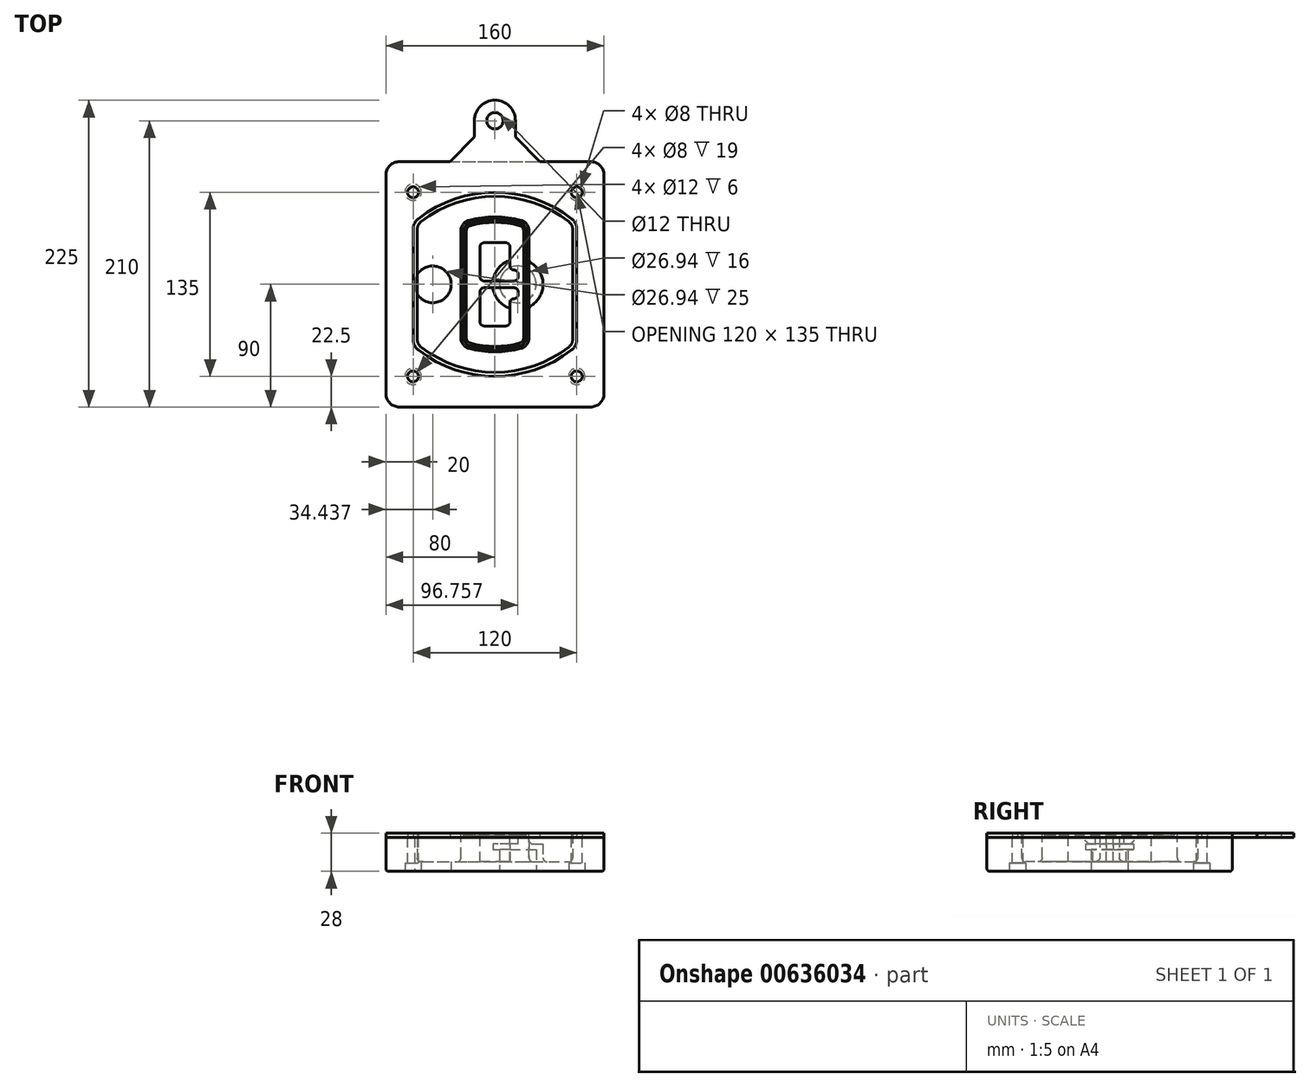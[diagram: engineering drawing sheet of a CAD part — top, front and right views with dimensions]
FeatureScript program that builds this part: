
annotation { "Feature Type Name" : "Feature", "Feature Type Description" : "" }
export const myFeature = defineFeature(function(context is Context, id is Id, definition is map)
    precondition{}
    {
        {
            var Q0;
            Q0=qCreatedBy(makeId("Top.planeOp"),FACE);
            var sketch = newSketch(context, id + "F0", { "sketchPlane" : qUnion([Q0])});
            skPoint(sketch, "E0.rect.middle", {"position": v(0, 0) * mm});
            skLineSegment(sketch, "E1.bottom", {"start": v(-70, -90) * mm, "end": v(70, -90) * mm});
            skLineSegment(sketch, "E1.top", {"start": v(-70, 90) * mm, "end": v(70, 90) * mm});
            skLineSegment(sketch, "E1.left", {"start": v(-80, -80) * mm, "end": v(-80, 80) * mm});
            skLineSegment(sketch, "E1.right", {"start": v(80, -80) * mm, "end": v(80, 80) * mm});
            skLineSegment(sketch, "E2", {"start": v(-80, 90) * mm, "end": v(80, -90) * mm, "construction": true});
            skLineSegment(sketch, "E3", {"start": v(80, 90) * mm, "end": v(-80, -90) * mm, "construction": true});
            skCircle(sketch, "E4", {"center": v(-60, 67.5) * mm, "radius": 4 * mm});
            skCircle(sketch, "E5", {"center": v(60, 67.5) * mm, "radius": 4 * mm});
            skCircle(sketch, "E6", {"center": v(60, -67.5) * mm, "radius": 4 * mm});
            skCircle(sketch, "E7", {"center": v(-60, -67.5) * mm, "radius": 4 * mm});
            skLineSegment(sketch, "E8", {"start": v(-60, 67.5) * mm, "end": v(60, 67.5) * mm, "construction": true});
            skLineSegment(sketch, "E9", {"start": v(60, 67.5) * mm, "end": v(60, -67.5) * mm, "construction": true});
            skLineSegment(sketch, "E10", {"start": v(60, -67.5) * mm, "end": v(-60, -67.5) * mm, "construction": true});
            skLineSegment(sketch, "E11", {"start": v(-60, -67.5) * mm, "end": v(-60, 67.5) * mm, "construction": true});
            skLineSegment(sketch, "E12", {"start": v(-60, 40.3) * mm, "end": v(-60, -40.3) * mm});
            skLineSegment(sketch, "E13", {"start": v(60, 40.3) * mm, "end": v(60, -40.3) * mm});
            skArc(sketch, "E14", {"start": v(56.15, 48.18) * mm, "mid": v(0, 67.5) * mm, "end": v(-56.15, 48.18) * mm});
            skArc(sketch, "E15", {"start": v(-56.15, -48.18) * mm, "mid": v(0, -67.5) * mm, "end": v(56.15, -48.18) * mm});
            skLineSegment(sketch, "E16", {"start": v(-60, 0) * mm, "end": v(60, 0) * mm, "construction": true});
            skPoint(sketch, "E17.visualSharp", {"position": v(-60, -45) * mm});
            skArc(sketch, "E17.filletArc", {"start": v(-60, -40.3) * mm, "mid": v(-58.99, -44.68) * mm, "end": v(-56.15, -48.18) * mm});
            skPoint(sketch, "E18.visualSharp", {"position": v(-60, 45) * mm});
            skArc(sketch, "E18.filletArc", {"start": v(-56.15, 48.18) * mm, "mid": v(-58.99, 44.68) * mm, "end": v(-60, 40.3) * mm});
            skPoint(sketch, "E19.visualSharp", {"position": v(60, 45) * mm});
            skArc(sketch, "E19.filletArc", {"start": v(60, 40.3) * mm, "mid": v(58.99, 44.68) * mm, "end": v(56.15, 48.18) * mm});
            skPoint(sketch, "E20.visualSharp", {"position": v(60, -45) * mm});
            skArc(sketch, "E20.filletArc", {"start": v(56.15, -48.18) * mm, "mid": v(58.99, -44.68) * mm, "end": v(60, -40.3) * mm});
            skPoint(sketch, "E21.visualSharp", {"position": v(-80, 90) * mm});
            skArc(sketch, "E21.filletArc", {"start": v(-70, 90) * mm, "mid": v(-77.07, 87.07) * mm, "end": v(-80, 80) * mm});
            skPoint(sketch, "E22.visualSharp", {"position": v(80, 90) * mm});
            skArc(sketch, "E22.filletArc", {"start": v(80, 80) * mm, "mid": v(77.07, 87.07) * mm, "end": v(70, 90) * mm});
            skPoint(sketch, "E23.visualSharp", {"position": v(80, -90) * mm});
            skArc(sketch, "E23.filletArc", {"start": v(70, -90) * mm, "mid": v(77.07, -87.07) * mm, "end": v(80, -80) * mm});
            skPoint(sketch, "E24.visualSharp", {"position": v(-80, -90) * mm});
            skArc(sketch, "E24.filletArc", {"start": v(-80, -80) * mm, "mid": v(-77.07, -87.07) * mm, "end": v(-70, -90) * mm});
            skArc(sketch, "E25.0", {"start": v(57, 40.3) * mm, "mid": v(56.3, 43.36) * mm, "end": v(54.3, 45.81) * mm});
            skLineSegment(sketch, "E25.1", {"start": v(57, 40.3) * mm, "end": v(57, -40.3) * mm});
            skArc(sketch, "E25.2", {"start": v(54.3, -45.81) * mm, "mid": v(56.3, -43.36) * mm, "end": v(57, -40.3) * mm});
            skArc(sketch, "E25.3", {"start": v(-54.3, -45.81) * mm, "mid": v(0, -64.5) * mm, "end": v(54.3, -45.81) * mm});
            skArc(sketch, "E25.4", {"start": v(-57, -40.3) * mm, "mid": v(-56.3, -43.36) * mm, "end": v(-54.3, -45.81) * mm});
            skArc(sketch, "E25.5", {"start": v(54.3, 45.81) * mm, "mid": v(0, 64.5) * mm, "end": v(-54.3, 45.81) * mm});
            skLineSegment(sketch, "E25.6", {"start": v(-57, 40.3) * mm, "end": v(-57, -40.3) * mm});
            skArc(sketch, "E25.7", {"start": v(-54.3, 45.81) * mm, "mid": v(-56.3, 43.36) * mm, "end": v(-57, 40.3) * mm});
            skArc(sketch, "E26.0", {"start": v(-58.62, 51.33) * mm, "mid": v(-62.58, 46.43) * mm, "end": v(-64, 40.3) * mm});
            skArc(sketch, "E26.1", {"start": v(58.62, 51.33) * mm, "mid": v(0, 71.5) * mm, "end": v(-58.62, 51.33) * mm});
            skArc(sketch, "E26.2", {"start": v(64, 40.3) * mm, "mid": v(62.58, 46.43) * mm, "end": v(58.62, 51.33) * mm});
            skLineSegment(sketch, "E26.3", {"start": v(64, 40.3) * mm, "end": v(64, -40.3) * mm});
            skArc(sketch, "E26.4", {"start": v(58.62, -51.33) * mm, "mid": v(62.58, -46.43) * mm, "end": v(64, -40.3) * mm});
            skLineSegment(sketch, "E26.5", {"start": v(-64, 40.3) * mm, "end": v(-64, -40.3) * mm});
            skArc(sketch, "E26.6", {"start": v(-58.62, -51.33) * mm, "mid": v(0, -71.5) * mm, "end": v(58.62, -51.33) * mm});
            skArc(sketch, "E26.7", {"start": v(-64, -40.3) * mm, "mid": v(-62.58, -46.43) * mm, "end": v(-58.62, -51.33) * mm});
            skSolve(sketch);
        }
        {
            var Q0;
            Q0=makeQuery(id+"F0.imprint","IMPRINT",FACE,{"disambiguationData":[TD([[makeQuery(id+"F0.imprint","IMPRINT",EDGE,{"derivedFrom":sQuery(id+"F0.wireOp",EDGE,"E1.bottom")}),1.0]])]});
            var Q1;
            Q1=makeQuery(id+"F0.imprint","IMPRINT",FACE,{"disambiguationData":[TD([[makeQuery(id+"F0.imprint","IMPRINT",EDGE,{"derivedFrom":sQuery(id+"F0.wireOp",EDGE,"E12")}),1.0]])]});
            var Q2;
            Q2=makeQuery(id+"F0.imprint","IMPRINT",FACE,{"disambiguationData":[TD([[makeQuery(id+"F0.imprint","IMPRINT",EDGE,{"derivedFrom":sQuery(id+"F0.wireOp",EDGE,"E25.0")}),1.0]])]});
            var Q3;
            Q3=makeQuery(id+"F0.imprint","IMPRINT",FACE,{"disambiguationData":[TD([[makeQuery(id+"F0.imprint","IMPRINT",EDGE,{"derivedFrom":sQuery(id+"F0.wireOp",EDGE,"E12")}),-1.0]])]});
            extrude(context, id + "F1", {"entities" : qUnion([Q0, Q1, Q2, Q3]), "oppositeDirection" : true, "depth" : 25 * mm});
        }
        {
            var Q0;
            Q0=makeQuery(id+"F0.imprint","IMPRINT",FACE,{"disambiguationData":[TD([[makeQuery(id+"F0.imprint","IMPRINT",EDGE,{"derivedFrom":sQuery(id+"F0.wireOp",EDGE,"E12")}),1.0]])]});
            extrude(context, id + "F2", {"entities" : qUnion([Q0]), "operationType" : NewBodyOperationType.ADD, "depth" : 3 * mm});
        }
        {
            var Q0;
            Q0=makeQuery(id+"F0.imprint","IMPRINT",FACE,{"disambiguationData":[TD([[makeQuery(id+"F0.imprint","IMPRINT",EDGE,{"derivedFrom":sQuery(id+"F0.wireOp",EDGE,"E25.0")}),1.0]])]});
            extrude(context, id + "F3", {"entities" : qUnion([Q0]), "operationType" : NewBodyOperationType.REMOVE, "oppositeDirection" : true, "depth" : 18 * mm});
        }
        {
            var Q0;
            Q0=makeQuery(id+"F2.opExtrude","CAP_FACE",FACE,{"disambiguationData":[OSD([sQuery(id+"F0.wireOp",EDGE,"E12"),sQuery(id+"F0.wireOp",EDGE,"E13"),sQuery(id+"F0.wireOp",EDGE,"E14"),sQuery(id+"F0.wireOp",EDGE,"E15"),sQuery(id+"F0.wireOp",EDGE,"E17.filletArc"),sQuery(id+"F0.wireOp",EDGE,"E18.filletArc"),sQuery(id+"F0.wireOp",EDGE,"E19.filletArc"),sQuery(id+"F0.wireOp",EDGE,"E20.filletArc"),sQuery(id+"F0.wireOp",EDGE,"E25.0"),sQuery(id+"F0.wireOp",EDGE,"E25.1"),sQuery(id+"F0.wireOp",EDGE,"E25.2"),sQuery(id+"F0.wireOp",EDGE,"E25.3"),sQuery(id+"F0.wireOp",EDGE,"E25.4"),sQuery(id+"F0.wireOp",EDGE,"E25.5"),sQuery(id+"F0.wireOp",EDGE,"E25.6"),sQuery(id+"F0.wireOp",EDGE,"E25.7")])],"isStart":false});
            var sketch = newSketch(context, id + "F4", { "sketchPlane" : qUnion([Q0])});
            skArc(sketch, "E27.0", {"start": v(-19.08, -46.97) * mm, "mid": v(0, -49.5) * mm, "end": v(19.08, -46.97) * mm});
            skArc(sketch, "E28.0", {"start": v(19.08, 46.97) * mm, "mid": v(0, 49.5) * mm, "end": v(-19.08, 46.97) * mm});
            skLineSegment(sketch, "E29", {"start": v(-25, 39.25) * mm, "end": v(-25, -39.25) * mm});
            skLineSegment(sketch, "E30", {"start": v(25, 39.25) * mm, "end": v(25, -39.25) * mm});
            skLineSegment(sketch, "E31", {"start": v(-25, 45.1) * mm, "end": v(25, 45.1) * mm, "construction": true});
            skLineSegment(sketch, "E32", {"start": v(-25, -45.1) * mm, "end": v(25, -45.1) * mm, "construction": true});
            skPoint(sketch, "E33.visualSharp", {"position": v(-25, 45.1) * mm});
            skArc(sketch, "E33.filletArc", {"start": v(-19.08, 46.97) * mm, "mid": v(-23.35, 44.11) * mm, "end": v(-25, 39.25) * mm});
            skPoint(sketch, "E34.visualSharp", {"position": v(25, 45.1) * mm});
            skArc(sketch, "E34.filletArc", {"start": v(25, 39.25) * mm, "mid": v(23.35, 44.11) * mm, "end": v(19.08, 46.97) * mm});
            skPoint(sketch, "E35.visualSharp", {"position": v(25, -45.1) * mm});
            skArc(sketch, "E35.filletArc", {"start": v(19.08, -46.97) * mm, "mid": v(23.35, -44.11) * mm, "end": v(25, -39.25) * mm});
            skPoint(sketch, "E36.visualSharp", {"position": v(-25, -45.1) * mm});
            skArc(sketch, "E36.filletArc", {"start": v(-25, -39.25) * mm, "mid": v(-23.35, -44.11) * mm, "end": v(-19.08, -46.97) * mm});
            skArc(sketch, "E37.0", {"start": v(54.3, 45.81) * mm, "mid": v(0, 64.5) * mm, "end": v(-54.3, 45.81) * mm});
            skArc(sketch, "E37.1", {"start": v(-54.3, 45.81) * mm, "mid": v(-56.3, 43.36) * mm, "end": v(-57, 40.3) * mm});
            skLineSegment(sketch, "E37.2", {"start": v(-57, 40.3) * mm, "end": v(-57, -40.3) * mm});
            skArc(sketch, "E37.3", {"start": v(-57, -40.3) * mm, "mid": v(-56.3, -43.36) * mm, "end": v(-54.3, -45.81) * mm});
            skArc(sketch, "E37.4", {"start": v(-54.3, -45.81) * mm, "mid": v(0, -64.5) * mm, "end": v(54.3, -45.81) * mm});
            skArc(sketch, "E37.5", {"start": v(54.3, -45.81) * mm, "mid": v(56.3, -43.36) * mm, "end": v(57, -40.3) * mm});
            skLineSegment(sketch, "E37.6", {"start": v(57, 40.3) * mm, "end": v(57, -40.3) * mm});
            skArc(sketch, "E37.7", {"start": v(57, 40.3) * mm, "mid": v(56.3, 43.36) * mm, "end": v(54.3, 45.81) * mm});
            skLineSegment(sketch, "E38.0", {"start": v(23, 39.25) * mm, "end": v(23, -39.25) * mm});
            skArc(sketch, "E38.1", {"start": v(18.56, -45.04) * mm, "mid": v(21.76, -42.9) * mm, "end": v(23, -39.25) * mm});
            skArc(sketch, "E38.2", {"start": v(-18.56, -45.04) * mm, "mid": v(0, -47.5) * mm, "end": v(18.56, -45.04) * mm});
            skArc(sketch, "E38.3", {"start": v(-23, -39.25) * mm, "mid": v(-21.76, -42.9) * mm, "end": v(-18.56, -45.04) * mm});
            skLineSegment(sketch, "E38.4", {"start": v(-23, 39.25) * mm, "end": v(-23, -39.25) * mm});
            skArc(sketch, "E38.5", {"start": v(23, 39.25) * mm, "mid": v(21.76, 42.9) * mm, "end": v(18.56, 45.04) * mm});
            skArc(sketch, "E38.6", {"start": v(-18.56, 45.04) * mm, "mid": v(-21.76, 42.9) * mm, "end": v(-23, 39.25) * mm});
            skArc(sketch, "E38.7", {"start": v(18.56, 45.04) * mm, "mid": v(0, 47.5) * mm, "end": v(-18.56, 45.04) * mm});
            skArc(sketch, "E39.0", {"start": v(21, 39.25) * mm, "mid": v(20.18, 41.68) * mm, "end": v(18.04, 43.1) * mm});
            skLineSegment(sketch, "E39.1", {"start": v(21, 39.25) * mm, "end": v(21, -39.25) * mm});
            skArc(sketch, "E39.2", {"start": v(18.04, -43.1) * mm, "mid": v(20.18, -41.68) * mm, "end": v(21, -39.25) * mm});
            skArc(sketch, "E39.3", {"start": v(-18.04, -43.1) * mm, "mid": v(0, -45.5) * mm, "end": v(18.04, -43.1) * mm});
            skArc(sketch, "E39.4", {"start": v(-21, -39.25) * mm, "mid": v(-20.18, -41.68) * mm, "end": v(-18.04, -43.1) * mm});
            skArc(sketch, "E39.5", {"start": v(18.04, 43.1) * mm, "mid": v(0, 45.5) * mm, "end": v(-18.04, 43.1) * mm});
            skLineSegment(sketch, "E39.6", {"start": v(-21, 39.25) * mm, "end": v(-21, -39.25) * mm});
            skArc(sketch, "E39.7", {"start": v(-18.04, 43.1) * mm, "mid": v(-20.18, 41.68) * mm, "end": v(-21, 39.25) * mm});
            skLineSegment(sketch, "E40", {"start": v(-25, 0) * mm, "end": v(25, 0) * mm, "construction": true});
            skLineSegment(sketch, "E41", {"start": v(-11, 5.5) * mm, "end": v(-11, 27.5) * mm});
            skLineSegment(sketch, "E42", {"start": v(-8, 30.5) * mm, "end": v(8, 30.5) * mm});
            skLineSegment(sketch, "E43", {"start": v(11, 27.5) * mm, "end": v(11, 13.5) * mm});
            skLineSegment(sketch, "E44", {"start": v(14, 10.5) * mm, "end": v(14, 10.5) * mm});
            skLineSegment(sketch, "E45", {"start": v(17, 7.5) * mm, "end": v(17, 5.5) * mm});
            skLineSegment(sketch, "E46", {"start": v(14, 2.5) * mm, "end": v(-8, 2.5) * mm});
            skPoint(sketch, "E47.visualSharp", {"position": v(-11, 30.5) * mm});
            skArc(sketch, "E47.filletArc", {"start": v(-8, 30.5) * mm, "mid": v(-10.12, 29.62) * mm, "end": v(-11, 27.5) * mm});
            skPoint(sketch, "E48.visualSharp", {"position": v(11, 30.5) * mm});
            skArc(sketch, "E48.filletArc", {"start": v(11, 27.5) * mm, "mid": v(10.12, 29.62) * mm, "end": v(8, 30.5) * mm});
            skPoint(sketch, "E49.visualSharp", {"position": v(11, 10.5) * mm});
            skArc(sketch, "E49.filletArc", {"start": v(11, 13.5) * mm, "mid": v(11.88, 11.38) * mm, "end": v(14, 10.5) * mm});
            skPoint(sketch, "E50.visualSharp", {"position": v(17, 10.5) * mm});
            skArc(sketch, "E50.filletArc", {"start": v(17, 7.5) * mm, "mid": v(16.12, 9.62) * mm, "end": v(14, 10.5) * mm});
            skPoint(sketch, "E51.visualSharp", {"position": v(17, 2.5) * mm});
            skArc(sketch, "E51.filletArc", {"start": v(14, 2.5) * mm, "mid": v(16.12, 3.38) * mm, "end": v(17, 5.5) * mm});
            skPoint(sketch, "E52.visualSharp", {"position": v(-11, 2.5) * mm});
            skArc(sketch, "E52.filletArc", {"start": v(-11, 5.5) * mm, "mid": v(-10.12, 3.38) * mm, "end": v(-8, 2.5) * mm});
            skLineSegment(sketch, "E53.0.MirrorCS", {"start": v(14, -2.5) * mm, "end": v(-8, -2.5) * mm});
            skArc(sketch, "E54.0.MirrorCS", {"start": v(-11, -5.5) * mm, "mid": v(-10.12, -3.38) * mm, "end": v(-8, -2.5) * mm});
            skLineSegment(sketch, "E55.0.MirrorCS", {"start": v(-11, -5.5) * mm, "end": v(-11, -27.5) * mm});
            skArc(sketch, "E56.0.MirrorCS", {"start": v(-8, -30.5) * mm, "mid": v(-10.12, -29.62) * mm, "end": v(-11, -27.5) * mm});
            skLineSegment(sketch, "E57.0.MirrorCS", {"start": v(-8, -30.5) * mm, "end": v(8, -30.5) * mm});
            skArc(sketch, "E58.0.MirrorCS", {"start": v(11, -27.5) * mm, "mid": v(10.12, -29.62) * mm, "end": v(8, -30.5) * mm});
            skLineSegment(sketch, "E59.0.MirrorCS", {"start": v(11, -27.5) * mm, "end": v(11, -13.5) * mm});
            skArc(sketch, "E60.0.MirrorCS", {"start": v(11, -13.5) * mm, "mid": v(11.88, -11.38) * mm, "end": v(14, -10.5) * mm});
            skArc(sketch, "E61.0.MirrorCS", {"start": v(17, -7.5) * mm, "mid": v(16.12, -9.62) * mm, "end": v(14, -10.5) * mm});
            skLineSegment(sketch, "E62.0.MirrorCS", {"start": v(17, -7.5) * mm, "end": v(17, -5.5) * mm});
            skArc(sketch, "E63.0.MirrorCS", {"start": v(14, -2.5) * mm, "mid": v(16.12, -3.38) * mm, "end": v(17, -5.5) * mm});
            skSolve(sketch);
        }
        {
            var Q0;
            Q0=makeQuery(id+"F4.imprint","IMPRINT",FACE,{"disambiguationData":[TD([[makeQuery(id+"F4.imprint","IMPRINT",EDGE,{"derivedFrom":sQuery(id+"F4.wireOp",EDGE,"E27.0")}),1.0]])]});
            var Q1;
            Q1=makeQuery(id+"F4.imprint","IMPRINT",FACE,{"disambiguationData":[TD([[makeQuery(id+"F4.imprint","IMPRINT",EDGE,{"derivedFrom":sQuery(id+"F4.wireOp",EDGE,"E38.0")}),-1.0]])]});
            var Q2;
            Q2=makeQuery(id+"F4.imprint","IMPRINT",FACE,{"disambiguationData":[TD([[makeQuery(id+"F4.imprint","IMPRINT",EDGE,{"derivedFrom":sQuery(id+"F4.wireOp",EDGE,"E39.0")}),1.0]])]});
            extrude(context, id + "F5", {"entities" : qUnion([Q0, Q1, Q2]), "operationType" : NewBodyOperationType.ADD, "endBound" : BoundingType.UP_TO_NEXT, "oppositeDirection" : true, "depth" : 25 * mm});
        }
        {
            var Q0;
            Q0=makeQuery(id+"F4.imprint","IMPRINT",FACE,{"disambiguationData":[TD([[makeQuery(id+"F4.imprint","IMPRINT",EDGE,{"derivedFrom":sQuery(id+"F4.wireOp",EDGE,"E38.0")}),-1.0]])]});
            extrude(context, id + "F6", {"entities" : qUnion([Q0]), "operationType" : NewBodyOperationType.REMOVE, "oppositeDirection" : true, "depth" : 2 * mm});
        }
        {
            var Q0;
            Q0=makeQuery(id+"F1.opExtrude","CAP_FACE",FACE,{"disambiguationData":[OSD([sQuery(id+"F0.wireOp",EDGE,"E1.bottom"),sQuery(id+"F0.wireOp",EDGE,"E1.top"),sQuery(id+"F0.wireOp",EDGE,"E1.left"),sQuery(id+"F0.wireOp",EDGE,"E1.right"),sQuery(id+"F0.wireOp",EDGE,"E4"),sQuery(id+"F0.wireOp",EDGE,"E5"),sQuery(id+"F0.wireOp",EDGE,"E6"),sQuery(id+"F0.wireOp",EDGE,"E7"),sQuery(id+"F0.wireOp",EDGE,"E21.filletArc"),sQuery(id+"F0.wireOp",EDGE,"E22.filletArc"),sQuery(id+"F0.wireOp",EDGE,"E23.filletArc"),sQuery(id+"F0.wireOp",EDGE,"E24.filletArc")])],"isStart":false});
            var sketch = newSketch(context, id + "F7", { "sketchPlane" : qUnion([Q0])});
            skCircle(sketch, "E64", {"center": v(16.76, 0) * mm, "radius": 13.47 * mm});
            skCircle(sketch, "E65", {"center": v(-45.56, 0) * mm, "radius": 13.47 * mm});
            skLineSegment(sketch, "E66", {"start": v(80, 0) * mm, "end": v(-80, 0) * mm});
            skCircle(sketch, "E67", {"center": v(16.76, 0) * mm, "radius": 18.47 * mm});
            skCircle(sketch, "E68", {"center": v(60, -67.5) * mm, "radius": 6 * mm});
            skCircle(sketch, "E69", {"center": v(-60, -67.5) * mm, "radius": 6 * mm});
            skCircle(sketch, "E70", {"center": v(-60, 67.5) * mm, "radius": 6 * mm});
            skCircle(sketch, "E71", {"center": v(60, 67.5) * mm, "radius": 6 * mm});
            skSolve(sketch);
        }
        {
            var Q0;
            {var subQ1=sQuery(id+"F7.wireOp",EDGE,"E66");var subQ4=sQuery(id+"F7.wireOp",EDGE,"E64");var subQ6=makeQuery(id+"F7.imprint","INTERSECT",VERTEX,{"disambiguationData":[OD(0.0)],"derivedFrom":[subQ4,subQ1]});Q0=makeQuery(id+"F7.imprint","IMPRINT",FACE,{"disambiguationData":[TD([[makeQuery(id+"F7.imprint","IMPRINT",EDGE,{"disambiguationData":[TD([[subQ6,-1.0]])],"derivedFrom":subQ4}),-1.0]])]});}
            var Q1;
            {var subQ0=sQuery(id+"F7.wireOp",EDGE,"E66");var subQ1=sQuery(id+"F7.wireOp",EDGE,"E64");var subQ3=makeQuery(id+"F7.imprint","INTERSECT",VERTEX,{"disambiguationData":[OD(0.0)],"derivedFrom":[subQ1,subQ0]});Q1=makeQuery(id+"F7.imprint","IMPRINT",FACE,{"disambiguationData":[TD([[makeQuery(id+"F7.imprint","IMPRINT",EDGE,{"disambiguationData":[TD([[subQ3,-1.0]])],"derivedFrom":subQ1}),1.0]])]});}
            var Q2;
            {var subQ0=sQuery(id+"F7.wireOp",EDGE,"E66");var subQ1=sQuery(id+"F7.wireOp",EDGE,"E64");var subQ3=makeQuery(id+"F7.imprint","INTERSECT",VERTEX,{"disambiguationData":[OD(0.0)],"derivedFrom":[subQ1,subQ0]});Q2=makeQuery(id+"F7.imprint","IMPRINT",FACE,{"disambiguationData":[TD([[makeQuery(id+"F7.imprint","IMPRINT",EDGE,{"disambiguationData":[TD([[subQ3,1.0]])],"derivedFrom":subQ1}),1.0]])]});}
            var Q3;
            {var subQ1=sQuery(id+"F7.wireOp",EDGE,"E66");var subQ4=sQuery(id+"F7.wireOp",EDGE,"E64");var subQ6=makeQuery(id+"F7.imprint","INTERSECT",VERTEX,{"disambiguationData":[OD(0.0)],"derivedFrom":[subQ4,subQ1]});Q3=makeQuery(id+"F7.imprint","IMPRINT",FACE,{"disambiguationData":[TD([[makeQuery(id+"F7.imprint","IMPRINT",EDGE,{"disambiguationData":[TD([[subQ6,1.0]])],"derivedFrom":subQ4}),-1.0]])]});}
            extrude(context, id + "F8", {"entities" : qUnion([Q0, Q1, Q2, Q3]), "operationType" : NewBodyOperationType.ADD, "oppositeDirection" : true, "depth" : 20 * mm});
        }
        {
            var Q0;
            {var subQ0=sQuery(id+"F7.wireOp",EDGE,"E66");var subQ1=sQuery(id+"F7.wireOp",EDGE,"E64");var subQ3=makeQuery(id+"F7.imprint","INTERSECT",VERTEX,{"disambiguationData":[OD(0.0)],"derivedFrom":[subQ1,subQ0]});Q0=makeQuery(id+"F7.imprint","IMPRINT",FACE,{"disambiguationData":[TD([[makeQuery(id+"F7.imprint","IMPRINT",EDGE,{"disambiguationData":[TD([[subQ3,-1.0]])],"derivedFrom":subQ1}),1.0]])]});}
            var Q1;
            {var subQ0=sQuery(id+"F7.wireOp",EDGE,"E66");var subQ1=sQuery(id+"F7.wireOp",EDGE,"E64");var subQ3=makeQuery(id+"F7.imprint","INTERSECT",VERTEX,{"disambiguationData":[OD(0.0)],"derivedFrom":[subQ1,subQ0]});Q1=makeQuery(id+"F7.imprint","IMPRINT",FACE,{"disambiguationData":[TD([[makeQuery(id+"F7.imprint","IMPRINT",EDGE,{"disambiguationData":[TD([[subQ3,1.0]])],"derivedFrom":subQ1}),1.0]])]});}
            extrude(context, id + "F9", {"entities" : qUnion([Q0, Q1]), "operationType" : NewBodyOperationType.REMOVE, "oppositeDirection" : true, "depth" : 16 * mm});
        }
        {
            var Q0;
            {var subQ0=sQuery(id+"F7.wireOp",EDGE,"E66");var subQ1=sQuery(id+"F7.wireOp",EDGE,"E65");var subQ3=makeQuery(id+"F7.imprint","INTERSECT",VERTEX,{"disambiguationData":[OD(0.0)],"derivedFrom":[subQ1,subQ0]});Q0=makeQuery(id+"F7.imprint","IMPRINT",FACE,{"disambiguationData":[TD([[makeQuery(id+"F7.imprint","IMPRINT",EDGE,{"disambiguationData":[TD([[subQ3,-1.0]])],"derivedFrom":subQ1}),1.0]])]});}
            var Q1;
            {var subQ0=sQuery(id+"F7.wireOp",EDGE,"E66");var subQ1=sQuery(id+"F7.wireOp",EDGE,"E65");var subQ3=makeQuery(id+"F7.imprint","INTERSECT",VERTEX,{"disambiguationData":[OD(0.0)],"derivedFrom":[subQ1,subQ0]});Q1=makeQuery(id+"F7.imprint","IMPRINT",FACE,{"disambiguationData":[TD([[makeQuery(id+"F7.imprint","IMPRINT",EDGE,{"disambiguationData":[TD([[subQ3,1.0]])],"derivedFrom":subQ1}),1.0]])]});}
            extrude(context, id + "F10", {"entities" : qUnion([Q0, Q1]), "operationType" : NewBodyOperationType.REMOVE, "oppositeDirection" : true, "depth" : 25 * mm});
        }
        {
            var Q0;
            Q0=makeQuery(id+"F7.imprint","IMPRINT",FACE,{"disambiguationData":[TD([[makeQuery(id+"F7.imprint","IMPRINT",EDGE,{"derivedFrom":sQuery(id+"F7.wireOp",EDGE,"E68")}),1.0]])]});
            var Q1;
            Q1=makeQuery(id+"F7.imprint","IMPRINT",FACE,{"disambiguationData":[TD([[makeQuery(id+"F7.imprint","IMPRINT",EDGE,{"derivedFrom":makeQuery(id+"F1.opExtrude","CAP_EDGE",EDGE,{"disambiguationData":[OSD([sQuery(id+"F0.wireOp",EDGE,"E5")])],"isStart":false})}),-1.0]])]});
            var Q2;
            Q2=makeQuery(id+"F7.imprint","IMPRINT",FACE,{"disambiguationData":[TD([[makeQuery(id+"F7.imprint","IMPRINT",EDGE,{"derivedFrom":sQuery(id+"F7.wireOp",EDGE,"E69")}),1.0]])]});
            var Q3;
            Q3=makeQuery(id+"F7.imprint","IMPRINT",FACE,{"disambiguationData":[TD([[makeQuery(id+"F7.imprint","IMPRINT",EDGE,{"derivedFrom":makeQuery(id+"F1.opExtrude","CAP_EDGE",EDGE,{"disambiguationData":[OSD([sQuery(id+"F0.wireOp",EDGE,"E4")])],"isStart":false})}),-1.0]])]});
            var Q4;
            Q4=makeQuery(id+"F7.imprint","IMPRINT",FACE,{"disambiguationData":[TD([[makeQuery(id+"F7.imprint","IMPRINT",EDGE,{"derivedFrom":sQuery(id+"F7.wireOp",EDGE,"E70")}),1.0]])]});
            var Q5;
            Q5=makeQuery(id+"F7.imprint","IMPRINT",FACE,{"disambiguationData":[TD([[makeQuery(id+"F7.imprint","IMPRINT",EDGE,{"derivedFrom":makeQuery(id+"F1.opExtrude","CAP_EDGE",EDGE,{"disambiguationData":[OSD([sQuery(id+"F0.wireOp",EDGE,"E7")])],"isStart":false})}),-1.0]])]});
            var Q6;
            Q6=makeQuery(id+"F7.imprint","IMPRINT",FACE,{"disambiguationData":[TD([[makeQuery(id+"F7.imprint","IMPRINT",EDGE,{"derivedFrom":sQuery(id+"F7.wireOp",EDGE,"E71")}),1.0]])]});
            var Q7;
            Q7=makeQuery(id+"F7.imprint","IMPRINT",FACE,{"disambiguationData":[TD([[makeQuery(id+"F7.imprint","IMPRINT",EDGE,{"derivedFrom":makeQuery(id+"F1.opExtrude","CAP_EDGE",EDGE,{"disambiguationData":[OSD([sQuery(id+"F0.wireOp",EDGE,"E6")])],"isStart":false})}),-1.0]])]});
            extrude(context, id + "F11", {"entities" : qUnion([Q0, Q1, Q2, Q3, Q4, Q5, Q6, Q7]), "operationType" : NewBodyOperationType.REMOVE, "oppositeDirection" : true, "depth" : 6 * mm});
        }
        {
            var Q0;
            Q0=makeQuery(id+"F9.boolean.opBoolean","COPY",FACE,{"derivedFrom":makeQuery(id+"F9.opExtrude","CAP_FACE",FACE,{"disambiguationData":[OSD([sQuery(id+"F7.wireOp",EDGE,"E64")])],"isStart":false})});
            var sketch = newSketch(context, id + "F12", { "sketchPlane" : qUnion([Q0])});
            skArc(sketch, "E72.0", {"start": v(11, 17.55) * mm, "mid": v(2.57, 11.82) * mm, "end": v(-1.54, 2.5) * mm});
            skArc(sketch, "E72.1", {"start": v(-1.54, -2.5) * mm, "mid": v(2.57, -11.82) * mm, "end": v(11, -17.55) * mm});
            skLineSegment(sketch, "E73", {"start": v(-1.54, -2.5) * mm, "end": v(14, -2.5) * mm});
            skLineSegment(sketch, "E74.0", {"start": v(14, 2.5) * mm, "end": v(-1.54, 2.5) * mm});
            skArc(sketch, "E74.1", {"start": v(14, 2.5) * mm, "mid": v(16.12, 3.38) * mm, "end": v(17, 5.5) * mm});
            skLineSegment(sketch, "E74.2", {"start": v(17, 7.5) * mm, "end": v(17, 5.5) * mm});
            skArc(sketch, "E74.3", {"start": v(17, 7.5) * mm, "mid": v(16.12, 9.62) * mm, "end": v(14, 10.5) * mm});
            skArc(sketch, "E74.4", {"start": v(11, 13.5) * mm, "mid": v(11.88, 11.38) * mm, "end": v(14, 10.5) * mm});
            skLineSegment(sketch, "E74.5", {"start": v(11, 17.55) * mm, "end": v(11, 13.5) * mm});
            skLineSegment(sketch, "E74.7", {"start": v(14, -2.5) * mm, "end": v(-1.54, -2.5) * mm});
            skArc(sketch, "E74.8", {"start": v(14, -2.5) * mm, "mid": v(16.12, -3.38) * mm, "end": v(17, -5.5) * mm});
            skLineSegment(sketch, "E74.9", {"start": v(17, -7.5) * mm, "end": v(17, -5.5) * mm});
            skArc(sketch, "E74.10", {"start": v(17, -7.5) * mm, "mid": v(16.12, -9.62) * mm, "end": v(14, -10.5) * mm});
            skArc(sketch, "E74.11", {"start": v(11, -13.5) * mm, "mid": v(11.88, -11.38) * mm, "end": v(14, -10.5) * mm});
            skLineSegment(sketch, "E74.12", {"start": v(11, -17.55) * mm, "end": v(11, -13.5) * mm});
            skPoint(sketch, "E75.orphan", {"position": v(11, -27.5) * mm});
            skPoint(sketch, "E76.orphan", {"position": v(-8, -2.5) * mm});
            skPoint(sketch, "E77.orphan", {"position": v(-8, 2.5) * mm});
            skPoint(sketch, "E78.orphan", {"position": v(11, 27.5) * mm});
            skSolve(sketch);
        }
        {
            var Q0;
            {var subQ7=sQuery(id+"F12.wireOp",EDGE,"E72.0");var subQ14=sQuery(id+"F12.wireOp",EDGE,"E72.1");var subQ16=sQuery(id+"F12.wireOp",EDGE,"E74.1");var subQ18=sQuery(id+"F12.wireOp",EDGE,"E74.8");Q0=qUnion([makeQuery(id+"F12.imprint","IMPRINT",FACE,{"disambiguationData":[TD([[makeQuery(id+"F12.imprint","IMPRINT",EDGE,{"derivedFrom":subQ7}),1.0]])]}),makeQuery(id+"F12.imprint","IMPRINT",FACE,{"disambiguationData":[TD([[makeQuery(id+"F12.imprint","IMPRINT",EDGE,{"derivedFrom":subQ14}),1.0]])]}),makeQuery(id+"F12.imprint","IMPRINT",FACE,{"disambiguationData":[TD([[makeQuery(id+"F12.imprint","IMPRINT",EDGE,{"derivedFrom":subQ16}),1.0]])]}),makeQuery(id+"F12.imprint","IMPRINT",FACE,{"disambiguationData":[TD([[makeQuery(id+"F12.imprint","IMPRINT",EDGE,{"derivedFrom":subQ18}),-1.0]])]})]);}
            var Q1;
            Q1=makeQuery(id+"F5.boolean.opBoolean","SPLIT",FACE,{"disambiguationData":[TD([makeQuery(id+"F5.opExtrude","SWEPT_FACE",FACE,{"disambiguationData":[OSD([sQuery(id+"F4.wireOp",EDGE,"E41")])]})])],"derivedFrom":makeQuery(id+"F3.boolean.opBoolean","COPY",FACE,{"derivedFrom":makeQuery(id+"F3.opExtrude","CAP_FACE",FACE,{"disambiguationData":[OSD([sQuery(id+"F0.wireOp",EDGE,"E25.0"),sQuery(id+"F0.wireOp",EDGE,"E25.1"),sQuery(id+"F0.wireOp",EDGE,"E25.2"),sQuery(id+"F0.wireOp",EDGE,"E25.3"),sQuery(id+"F0.wireOp",EDGE,"E25.4"),sQuery(id+"F0.wireOp",EDGE,"E25.5"),sQuery(id+"F0.wireOp",EDGE,"E25.6"),sQuery(id+"F0.wireOp",EDGE,"E25.7")])],"isStart":false})})});
            extrude(context, id + "F13", {"entities" : qUnion([Q0]), "operationType" : NewBodyOperationType.REMOVE, "endBound" : BoundingType.UP_TO_SURFACE, "endBoundEntityFace" : qUnion([Q1]), "depth" : 25 * mm});
        }
        {
            var Q0;
            Q0=makeQuery(id+"F3.boolean.opBoolean","COPY",EDGE,{"derivedFrom":makeQuery(id+"F3.opExtrude","CAP_EDGE",EDGE,{"disambiguationData":[OSD([sQuery(id+"F0.wireOp",EDGE,"E25.6")])],"isStart":false})});
            var Q1;
            Q1=makeQuery(id+"F8.boolean.opBoolean","INTERSECT",EDGE,{"derivedFrom":[makeQuery(id+"F5.opExtrude","SWEPT_FACE",FACE,{"disambiguationData":[OSD([sQuery(id+"F4.wireOp",EDGE,"E30")])]}),makeQuery(id+"F8.opExtrude","CAP_FACE",FACE,{"disambiguationData":[OSD([sQuery(id+"F7.wireOp",EDGE,"E67")])],"isStart":false})]});
            var Q2;
            Q2=makeQuery(id+"F8.boolean.opBoolean","INTERSECT",EDGE,{"disambiguationData":[OD(1.0)],"derivedFrom":[makeQuery(id+"F5.opExtrude","SWEPT_FACE",FACE,{"disambiguationData":[OSD([sQuery(id+"F4.wireOp",EDGE,"E30")])]}),makeQuery(id+"F8.opExtrude","SWEPT_FACE",FACE,{"disambiguationData":[OSD([sQuery(id+"F7.wireOp",EDGE,"E67")])]})]});
            var Q3;
            {var subQ0=sQuery(id+"F4.wireOp",EDGE,"E30");Q3=makeQuery(id+"F8.boolean.opBoolean","SPLIT",EDGE,{"disambiguationData":[TD([makeQuery(id+"F5.opExtrude","SWEPT_FACE",FACE,{"disambiguationData":[OSD([sQuery(id+"F4.wireOp",EDGE,"E35.filletArc")])]})])],"derivedFrom":makeQuery(id+"F5.opExtrude","CAP_EDGE",EDGE,{"disambiguationData":[OSD([subQ0])],"isStart":false})});}
            var Q4;
            {var subQ0=sQuery(id+"F0.wireOp",EDGE,"E25.7");var subQ1=sQuery(id+"F0.wireOp",EDGE,"E25.1");var subQ2=sQuery(id+"F0.wireOp",EDGE,"E25.6");var subQ3=sQuery(id+"F0.wireOp",EDGE,"E25.5");var subQ4=sQuery(id+"F0.wireOp",EDGE,"E25.4");var subQ5=sQuery(id+"F0.wireOp",EDGE,"E25.0");var subQ6=sQuery(id+"F0.wireOp",EDGE,"E25.2");var subQ7=sQuery(id+"F0.wireOp",EDGE,"E25.3");Q4=makeQuery(id+"F8.boolean.opBoolean","INTERSECT",EDGE,{"derivedFrom":[makeQuery(id+"F5.boolean.opBoolean","SPLIT",FACE,{"disambiguationData":[TD([makeQuery(id+"F2.opExtrude","SWEPT_FACE",FACE,{"disambiguationData":[OSD([subQ5])]})])],"derivedFrom":makeQuery(id+"F3.boolean.opBoolean","COPY",FACE,{"derivedFrom":makeQuery(id+"F3.opExtrude","CAP_FACE",FACE,{"disambiguationData":[OSD([subQ5,subQ1,subQ6,subQ7,subQ4,subQ3,subQ2,subQ0])],"isStart":false})})}),makeQuery(id+"F8.opExtrude","SWEPT_FACE",FACE,{"disambiguationData":[OSD([sQuery(id+"F7.wireOp",EDGE,"E67")])]})]});}
            var Q5;
            Q5=makeQuery(id+"F8.boolean.opBoolean","INTERSECT",EDGE,{"disambiguationData":[OD(0.0)],"derivedFrom":[makeQuery(id+"F5.opExtrude","SWEPT_FACE",FACE,{"disambiguationData":[OSD([sQuery(id+"F4.wireOp",EDGE,"E30")])]}),makeQuery(id+"F8.opExtrude","SWEPT_FACE",FACE,{"disambiguationData":[OSD([sQuery(id+"F7.wireOp",EDGE,"E67")])]})]});
            fillet(context, id + "F14", {"entities" : qUnion([Q0, Q1, Q2, Q3, Q4, Q5]), "radius" : 3 * mm, "tangentPropagation" : true, "allowEdgeOverflow" : false});
        }
        {
            var Q0;
            Q0=makeQuery(id+"F1.opExtrude","CAP_EDGE",EDGE,{"disambiguationData":[OSD([sQuery(id+"F0.wireOp",EDGE,"E1.bottom")])],"isStart":false});
            fillet(context, id + "F15", {"entities" : qUnion([Q0]), "radius" : 2 * mm, "tangentPropagation" : true, "allowEdgeOverflow" : false});
        }
        {
            var Q0;
            {var subQ0=sQuery(id+"F0.wireOp",EDGE,"E22.filletArc");var subQ1=sQuery(id+"F0.wireOp",EDGE,"E7");var subQ2=sQuery(id+"F0.wireOp",EDGE,"E6");var subQ3=sQuery(id+"F0.wireOp",EDGE,"E5");var subQ4=sQuery(id+"F0.wireOp",EDGE,"E4");var subQ5=sQuery(id+"F0.wireOp",EDGE,"E1.bottom");var subQ6=sQuery(id+"F0.wireOp",EDGE,"E21.filletArc");var subQ7=sQuery(id+"F0.wireOp",EDGE,"E1.top");var subQ8=sQuery(id+"F0.wireOp",EDGE,"E1.left");var subQ9=sQuery(id+"F0.wireOp",EDGE,"E1.right");var subQ10=sQuery(id+"F0.wireOp",EDGE,"E23.filletArc");var subQ11=sQuery(id+"F0.wireOp",EDGE,"E24.filletArc");Q0=makeQuery(id+"F2.boolean.opBoolean","SPLIT",FACE,{"disambiguationData":[TD([makeQuery(id+"F1.opExtrude","SWEPT_FACE",FACE,{"disambiguationData":[OSD([subQ5])]})])],"derivedFrom":makeQuery(id+"F1.opExtrude","CAP_FACE",FACE,{"disambiguationData":[OSD([subQ5,subQ7,subQ8,subQ9,subQ4,subQ3,subQ2,subQ1,subQ6,subQ0,subQ10,subQ11])],"isStart":true})});}
            var sketch = newSketch(context, id + "F16", { "sketchPlane" : qUnion([Q0])});
            skLineSegment(sketch, "E79", {"start": v(-33, 90) * mm, "end": v(-15, 108) * mm});
            skLineSegment(sketch, "E80", {"start": v(33, 90) * mm, "end": v(15, 108) * mm});
            skLineSegment(sketch, "E81", {"start": v(-15, 108) * mm, "end": v(-15, 120) * mm});
            skLineSegment(sketch, "E82", {"start": v(15, 108) * mm, "end": v(15, 120) * mm});
            skArc(sketch, "E83", {"start": v(15, 120) * mm, "mid": v(0, 135) * mm, "end": v(-15, 120) * mm});
            skLineSegment(sketch, "E84", {"start": v(0, 120) * mm, "end": v(0, 90) * mm, "construction": true});
            skPoint(sketch, "E84.endSnap0", {"position": v(0, 90) * mm});
            skCircle(sketch, "E85", {"center": v(0, 120) * mm, "radius": 6 * mm});
            skLineSegment(sketch, "E86", {"start": v(-80, 0) * mm, "end": v(80, 0) * mm, "construction": true});
            skArc(sketch, "E87.MirrorCS", {"start": v(15, -120) * mm, "mid": v(0, -135) * mm, "end": v(-15, -120) * mm});
            skLineSegment(sketch, "E88.MirrorCS", {"start": v(-15, -108) * mm, "end": v(-15, -120) * mm});
            skLineSegment(sketch, "E89.MirrorCS", {"start": v(15, -108) * mm, "end": v(15, -120) * mm});
            skCircle(sketch, "E90.MirrorC", {"center": v(0, -120) * mm, "radius": 6 * mm});
            skLineSegment(sketch, "E91.MirrorCS", {"start": v(33, -90) * mm, "end": v(15, -108) * mm});
            skLineSegment(sketch, "E92.MirrorCS", {"start": v(-33, -90) * mm, "end": v(-15, -108) * mm});
            skLineSegment(sketch, "E93.MirrorCS", {"start": v(0, -120) * mm, "end": v(0, -90) * mm, "construction": true});
            skSolve(sketch);
        }
        {
            var Q0;
            {var subQ0=sQuery(id+"F16.wireOp",EDGE,"E79");Q0=makeQuery(id+"F16.imprint","IMPRINT",FACE,{"disambiguationData":[TD([[makeQuery(id+"F16.imprint","IMPRINT",EDGE,{"derivedFrom":subQ0}),-1.0]])]});}
            var Q1;
            Q1=makeQuery(id+"F16.imprint","IMPRINT",FACE,{"disambiguationData":[TD([[makeQuery(id+"F16.imprint","IMPRINT",EDGE,{"derivedFrom":makeQuery(id+"F1.opExtrude","CAP_EDGE",EDGE,{"disambiguationData":[OSD([sQuery(id+"F0.wireOp",EDGE,"E1.left")])],"isStart":true})}),-1.0]])]});
            var Q2;
            Q2=makeQuery(id+"F16.imprint","IMPRINT",FACE,{"disambiguationData":[TD([[makeQuery(id+"F16.imprint","IMPRINT",EDGE,{"derivedFrom":sQuery(id+"F16.wireOp",EDGE,"E87.MirrorCS")}),-1.0]])]});
            var Q3;
            Q3=makeQuery(id+"F2.opExtrude","CAP_FACE",FACE,{"disambiguationData":[OSD([sQuery(id+"F0.wireOp",EDGE,"E12"),sQuery(id+"F0.wireOp",EDGE,"E13"),sQuery(id+"F0.wireOp",EDGE,"E14"),sQuery(id+"F0.wireOp",EDGE,"E15"),sQuery(id+"F0.wireOp",EDGE,"E17.filletArc"),sQuery(id+"F0.wireOp",EDGE,"E18.filletArc"),sQuery(id+"F0.wireOp",EDGE,"E19.filletArc"),sQuery(id+"F0.wireOp",EDGE,"E20.filletArc"),sQuery(id+"F0.wireOp",EDGE,"E25.0"),sQuery(id+"F0.wireOp",EDGE,"E25.1"),sQuery(id+"F0.wireOp",EDGE,"E25.2"),sQuery(id+"F0.wireOp",EDGE,"E25.3"),sQuery(id+"F0.wireOp",EDGE,"E25.4"),sQuery(id+"F0.wireOp",EDGE,"E25.5"),sQuery(id+"F0.wireOp",EDGE,"E25.6"),sQuery(id+"F0.wireOp",EDGE,"E25.7")])],"isStart":false});
            extrude(context, id + "F17", {"entities" : qUnion([Q0, Q1, Q2]), "endBound" : BoundingType.UP_TO_SURFACE, "endBoundEntityFace" : qUnion([Q3]), "depth" : 25 * mm});
        }
    });
